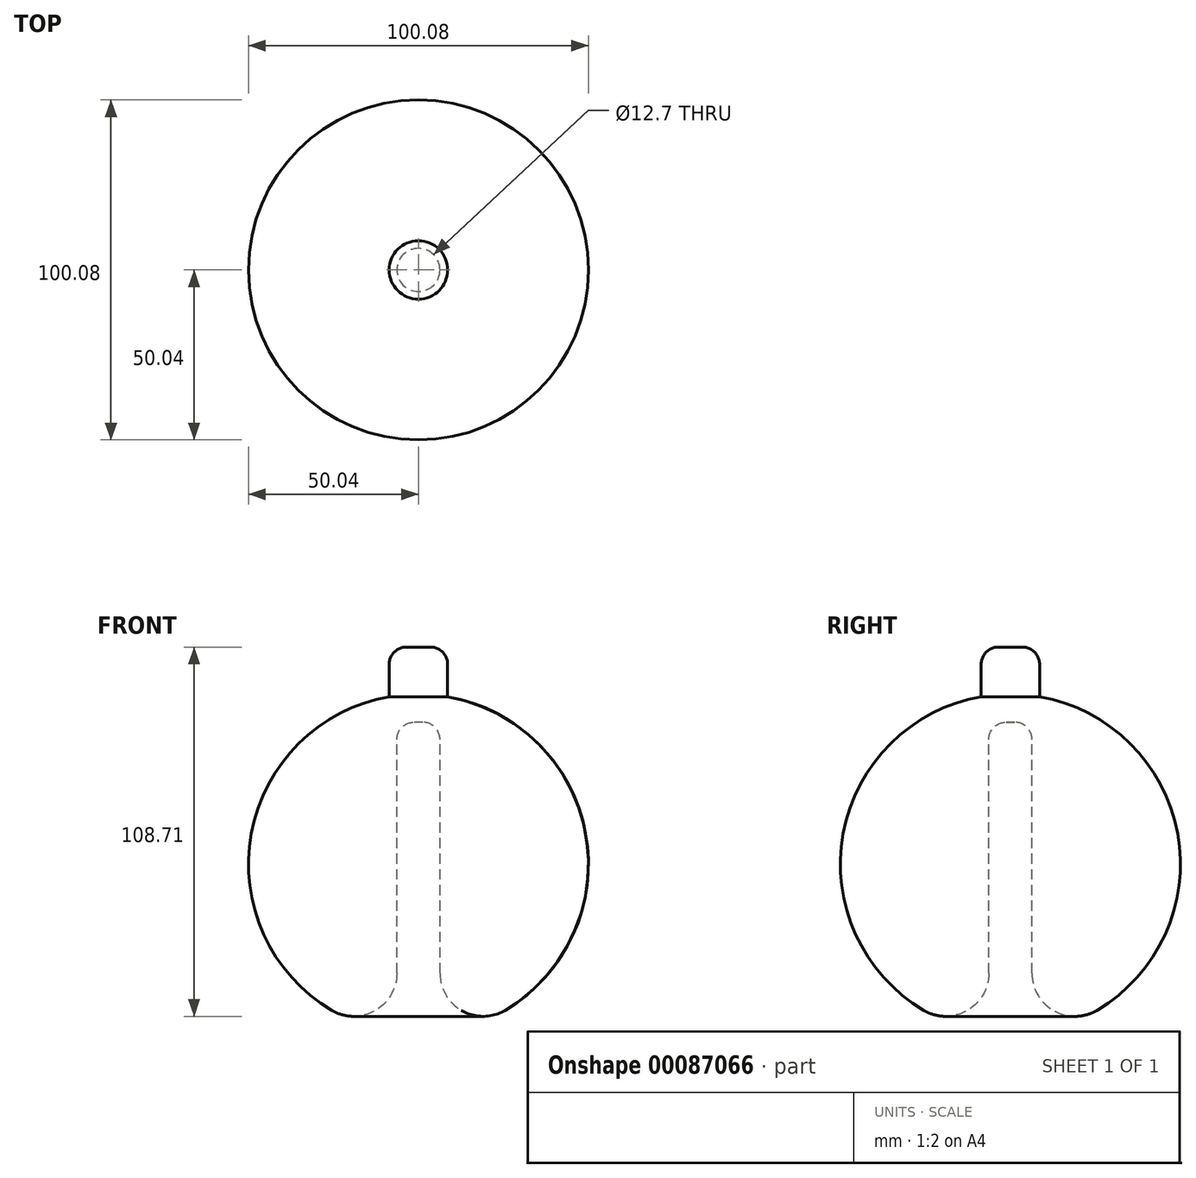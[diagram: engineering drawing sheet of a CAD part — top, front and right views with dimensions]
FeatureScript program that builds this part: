
annotation { "Feature Type Name" : "Feature", "Feature Type Description" : "" }
export const myFeature = defineFeature(function(context is Context, id is Id, definition is map)
    precondition{}
    {
        {
            var Q0;
            Q0=qCreatedBy(makeId("Front.planeOp"),FACE);
            var sketch = newSketch(context, id + "F0", { "sketchPlane" : qUnion([Q0])});
            skArc(sketch, "E0", {"start": v(0, 50.04) * mm, "mid": v(-50.04, 0) * mm, "end": v(0, -50.04) * mm});
            skLineSegment(sketch, "E1", {"start": v(0, 0) * mm, "end": v(0, 63.5) * mm});
            skLineSegment(sketch, "E2.bottom", {"start": v(0, 0) * mm, "end": v(-8.6, 0) * mm});
            skLineSegment(sketch, "E2.top", {"start": v(0, 63.9) * mm, "end": v(-8.6, 63.9) * mm});
            skLineSegment(sketch, "E2.left", {"start": v(0, 0) * mm, "end": v(0, 63.9) * mm});
            skLineSegment(sketch, "E2.right", {"start": v(-8.6, 0) * mm, "end": v(-8.6, 63.9) * mm});
            skLineSegment(sketch, "E3", {"start": v(0, 0) * mm, "end": v(0, -59.7) * mm});
            skSolve(sketch);
        }
        {
            var Q0;
            {var subQ5=sQuery(id+"F0.wireOp",EDGE,"E2.bottom");Q0=makeQuery(id+"F0.imprint","IMPRINT",FACE,{"disambiguationData":[TD([[makeQuery(id+"F0.imprint","IMPRINT",EDGE,{"derivedFrom":subQ5}),1.0]])]});}
            var Q1;
            {var subQ5=sQuery(id+"F0.wireOp",EDGE,"E2.bottom");Q1=makeQuery(id+"F0.imprint","IMPRINT",FACE,{"disambiguationData":[TD([[makeQuery(id+"F0.imprint","IMPRINT",EDGE,{"derivedFrom":subQ5}),-1.0]])]});}
            var Q2;
            Q2=sQuery(id+"F0.wireOp",EDGE,"E3");
            revolve(context, id + "F1", {"entities" : qUnion([Q0, Q1]), "axis" : qUnion([Q2]), "revolveType" : RevolveType.FULL});
        }
        {
            var Q0;
            {var subQ5=sQuery(id+"F0.wireOp",EDGE,"E2.top");Q0=makeQuery(id+"F0.imprint","IMPRINT",FACE,{"disambiguationData":[TD([[makeQuery(id+"F0.imprint","IMPRINT",EDGE,{"derivedFrom":subQ5}),1.0]])]});}
            var Q1;
            Q1=sQuery(id+"F0.wireOp",EDGE,"E3");
            revolve(context, id + "F2", {"operationType" : NewBodyOperationType.ADD, "entities" : qUnion([Q0]), "axis" : qUnion([Q1]), "revolveType" : RevolveType.FULL});
        }
        {
            var Q0;
            Q0=makeQuery(id+"F2.opRevolve","SWEPT_EDGE",EDGE,{"disambiguationData":[OSD([sQuery(id+"F0.wireOp",EDGE,"E0"),sQuery(id+"F0.wireOp",EDGE,"E2.right")])]});
            var Q1;
            Q1=makeQuery(id+"F2.opRevolve","SWEPT_EDGE",EDGE,{"disambiguationData":[OSD([sQuery(id+"F0.wireOp",EDGE,"E2.top"),sQuery(id+"F0.wireOp",EDGE,"E2.right")])]});
            fillet(context, id + "F3", {"entities" : qUnion([Q0, Q1]), "radius" : 5.08 * mm, "tangentPropagation" : true, "allowEdgeOverflow" : false});
        }
        {
            var Q0;
            Q0=qCreatedBy(makeId("Top.planeOp"),FACE);
            var sketch = newSketch(context, id + "F4", { "sketchPlane" : qUnion([Q0])});
            skCircle(sketch, "E4", {"center": v(0, 0) * mm, "radius": 6.35 * mm});
            skSolve(sketch);
        }
        {
            var Q0;
            Q0 = qSketchRegion(id + "F4", true);
            extrude(context, id + "F5", {"entities" : qUnion([Q0]), "operationType" : NewBodyOperationType.REMOVE, "oppositeDirection" : true, "depth" : 172.62 * mm});
        }
        {
            var Q0;
            Q0 = qSketchRegion(id + "F4", true);
            extrude(context, id + "F6", {"entities" : qUnion([Q0]), "operationType" : NewBodyOperationType.REMOVE, "depth" : 41.77 * mm});
        }
        {
            var Q0;
            Q0=makeQuery(id+"F6.boolean.opBoolean","COPY",EDGE,{"derivedFrom":makeQuery(id+"F6.opExtrude","CAP_EDGE",EDGE,{"disambiguationData":[OSD([sQuery(id+"F4.wireOp",EDGE,"E4")])],"isStart":false})});
            fillet(context, id + "F7", {"entities" : qUnion([Q0]), "radius" : 5.08 * mm, "tangentPropagation" : true, "allowEdgeOverflow" : false});
        }
        {
            var Q0;
            Q0=makeQuery(id+"F5.boolean.opBoolean","INTERSECT",EDGE,{"derivedFrom":[makeQuery(id+"F1.opRevolve","SWEPT_FACE",FACE,{"disambiguationData":[OSD([sQuery(id+"F0.wireOp",EDGE,"E0")])]}),makeQuery(id+"F5.opExtrude","SWEPT_FACE",FACE,{"disambiguationData":[OSD([sQuery(id+"F4.wireOp",EDGE,"E4")])]})]});
            fillet(context, id + "F8", {"entities" : qUnion([Q0]), "radius" : 12.7 * mm, "tangentPropagation" : true, "allowEdgeOverflow" : false});
        }
    });
